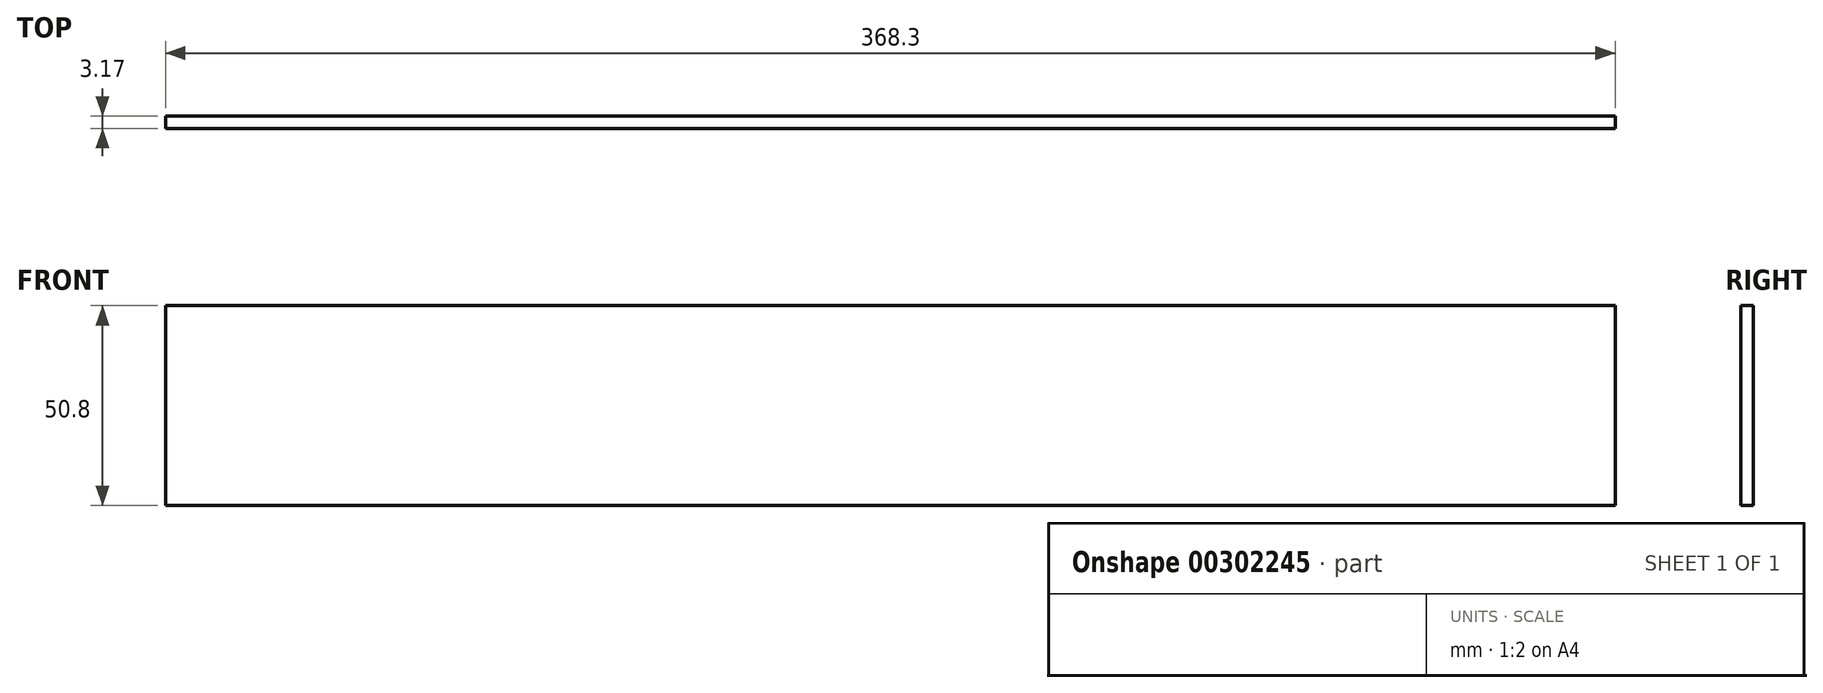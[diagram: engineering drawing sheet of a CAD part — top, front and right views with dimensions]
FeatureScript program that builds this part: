
annotation { "Feature Type Name" : "Feature", "Feature Type Description" : "" }
export const myFeature = defineFeature(function(context is Context, id is Id, definition is map)
    precondition{}
    {
        {
            var Q0;
            Q0=qCreatedBy(makeId("Front.planeOp"),FACE);
            var sketch = newSketch(context, id + "F0", { "sketchPlane" : qUnion([Q0])});
            skLineSegment(sketch, "E0.bottom", {"start": v(0, 0) * mm, "end": v(368.3, 0) * mm});
            skLineSegment(sketch, "E0.top", {"start": v(0, 50.8) * mm, "end": v(368.3, 50.8) * mm});
            skLineSegment(sketch, "E0.left", {"start": v(0, 0) * mm, "end": v(0, 50.8) * mm});
            skLineSegment(sketch, "E0.right", {"start": v(368.3, 0) * mm, "end": v(368.3, 50.8) * mm});
            skSolve(sketch);
        }
        {
            var Q0;
            Q0=makeQuery(id+"F0.imprint","IMPRINT",FACE,{"disambiguationData":[TD([[makeQuery(id+"F0.imprint","IMPRINT",EDGE,{"derivedFrom":sQuery(id+"F0.wireOp",EDGE,"E0.bottom")}),1.0]])]});
            extrude(context, id + "F1", {"entities" : qUnion([Q0]), "depth" : 3.17 * mm});
        }
    });
